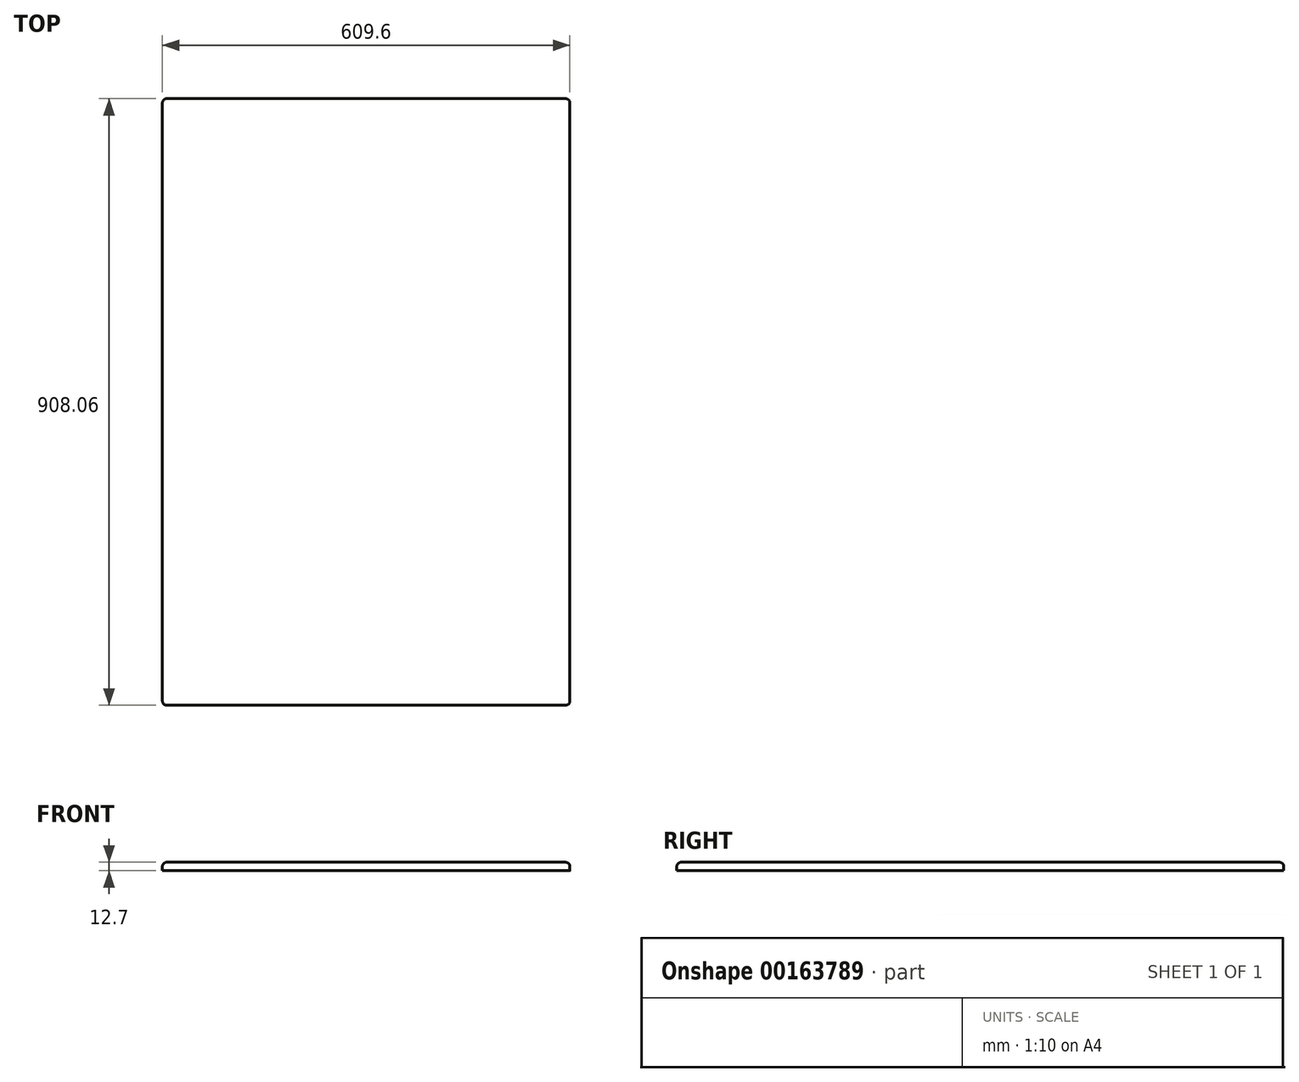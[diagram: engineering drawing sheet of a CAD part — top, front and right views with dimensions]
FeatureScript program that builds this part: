
annotation { "Feature Type Name" : "Feature", "Feature Type Description" : "" }
export const myFeature = defineFeature(function(context is Context, id is Id, definition is map)
    precondition{}
    {
        {
            var Q0;
            Q0=qCreatedBy(makeId("Top.planeOp"),FACE);
            var sketch = newSketch(context, id + "F0", { "sketchPlane" : qUnion([Q0])});
            skLineSegment(sketch, "E0.bottom", {"start": v(298.45, -454.03) * mm, "end": v(-298.45, -454.03) * mm});
            skLineSegment(sketch, "E0.top", {"start": v(298.45, 454.03) * mm, "end": v(-298.45, 454.03) * mm});
            skLineSegment(sketch, "E0.left", {"start": v(304.8, -447.68) * mm, "end": v(304.8, 447.68) * mm});
            skLineSegment(sketch, "E0.right", {"start": v(-304.8, -447.68) * mm, "end": v(-304.8, 447.68) * mm});
            skPoint(sketch, "E0.middle", {"position": v(0, 0) * mm});
            skPoint(sketch, "E1.visualSharp", {"position": v(304.8, 454.03) * mm});
            skArc(sketch, "E1.filletArc", {"start": v(304.8, 447.68) * mm, "mid": v(302.94, 452.17) * mm, "end": v(298.45, 454.03) * mm});
            skPoint(sketch, "E2.visualSharp", {"position": v(-304.8, 454.03) * mm});
            skArc(sketch, "E2.filletArc", {"start": v(-298.45, 454.03) * mm, "mid": v(-302.94, 452.17) * mm, "end": v(-304.8, 447.68) * mm});
            skPoint(sketch, "E3.visualSharp", {"position": v(-304.8, -454.03) * mm});
            skArc(sketch, "E3.filletArc", {"start": v(-304.8, -447.68) * mm, "mid": v(-302.94, -452.17) * mm, "end": v(-298.45, -454.03) * mm});
            skPoint(sketch, "E4.visualSharp", {"position": v(304.8, -454.03) * mm});
            skArc(sketch, "E4.filletArc", {"start": v(298.45, -454.03) * mm, "mid": v(302.94, -452.17) * mm, "end": v(304.8, -447.68) * mm});
            skSolve(sketch);
        }
        {
            var Q0;
            Q0=qSketchRegion(id+"F0",true);
            extrude(context, id + "F1", {"entities" : qUnion([Q0]), "depth" : 12.7 * mm});
        }
        {
            var Q0;
            Q0=makeQuery(id+"F1.opExtrude","CAP_EDGE",EDGE,{"disambiguationData":[OSD([sQuery(id+"F0.wireOp",EDGE,"E0.right")])],"isStart":false});
            fillet(context, id + "F2", {"entities" : qUnion([Q0]), "radius" : 6.35 * mm, "tangentPropagation" : true, "allowEdgeOverflow" : false});
        }
    });
